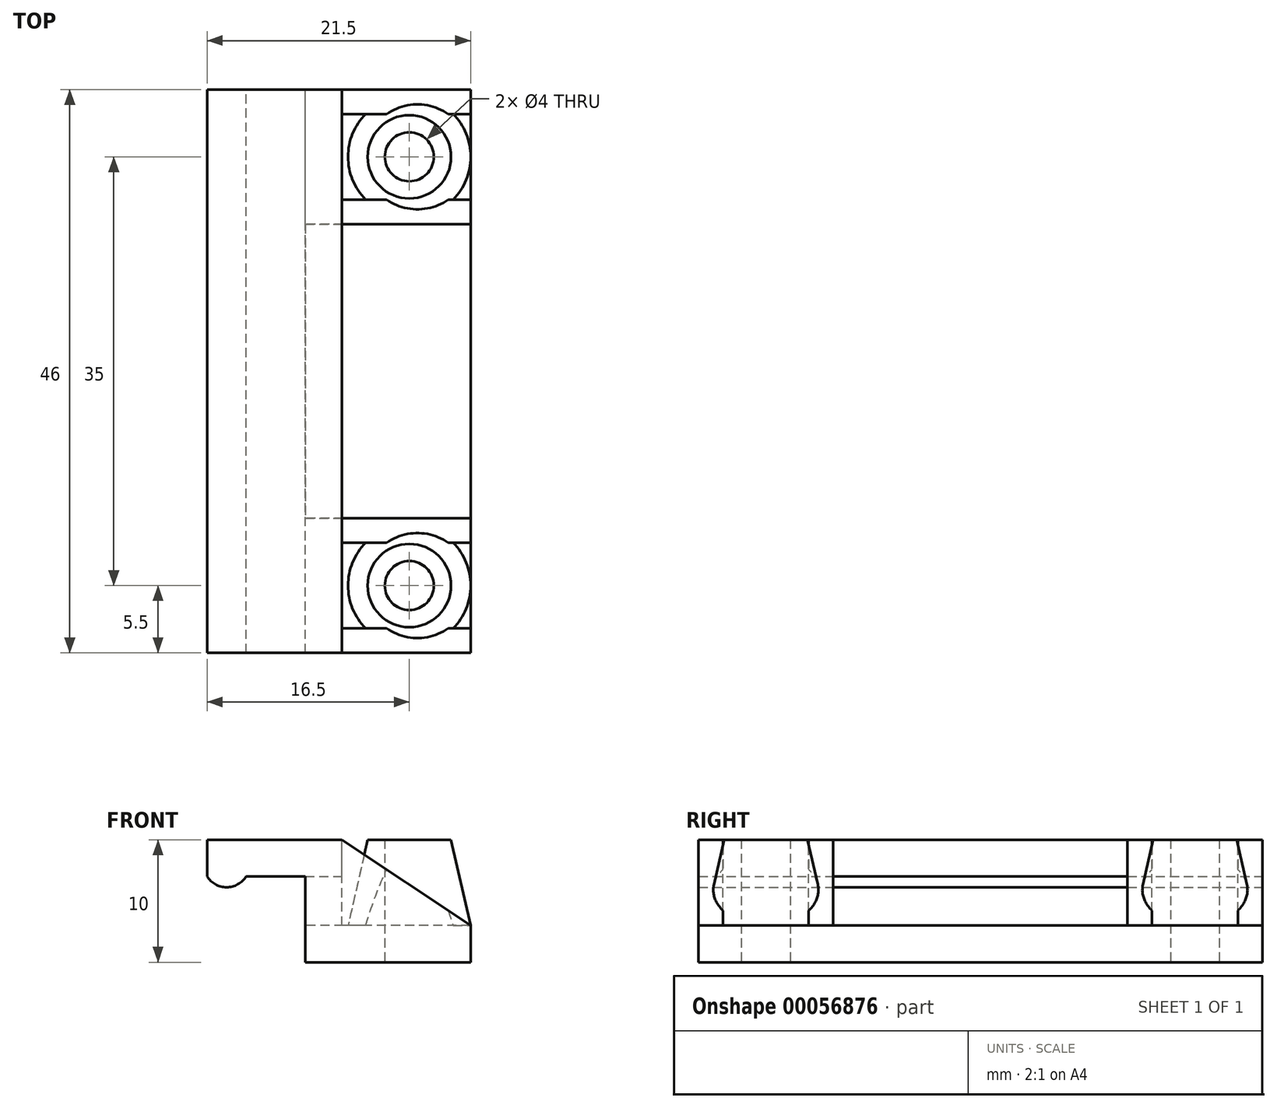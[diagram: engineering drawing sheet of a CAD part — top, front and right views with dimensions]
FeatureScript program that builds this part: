
annotation { "Feature Type Name" : "Feature", "Feature Type Description" : "" }
export const myFeature = defineFeature(function(context is Context, id is Id, definition is map)
    precondition{}
    {
        {
            var Q0;
            Q0=qCreatedBy(makeId("Front.planeOp"),FACE);
            var sketch = newSketch(context, id + "F0", { "sketchPlane" : qUnion([Q0])});
            skLineSegment(sketch, "E0", {"start": v(57.42, 0) * mm, "end": v(-61.71, 0) * mm, "construction": true});
            skLineSegment(sketch, "E1", {"start": v(0, 5) * mm, "end": v(0, -5) * mm, "construction": true});
            skLineSegment(sketch, "E2.0", {"start": v(12, 5) * mm, "end": v(-9.5, 5) * mm});
            skLineSegment(sketch, "E3.0", {"start": v(12, -5) * mm, "end": v(-9.5, -5) * mm});
            skPoint(sketch, "E4.orphan", {"position": v(0, 44.91) * mm});
            skLineSegment(sketch, "E5.0", {"start": v(-9.5, 5) * mm, "end": v(-9.5, -5) * mm, "construction": true});
            skLineSegment(sketch, "E6.0", {"start": v(12, 5) * mm, "end": v(12, -5) * mm, "construction": true});
            skLineSegment(sketch, "E7.0", {"start": v(1.5, 4) * mm, "end": v(1.5, -4) * mm, "construction": true});
            skLineSegment(sketch, "E8.0", {"start": v(-1.5, 4) * mm, "end": v(-1.5, -4) * mm, "construction": true});
            skLineSegment(sketch, "E9.0", {"start": v(57.42, 2) * mm, "end": v(-61.71, 2) * mm, "construction": true});
            skLineSegment(sketch, "E10.0", {"start": v(57.42, -2) * mm, "end": v(-61.71, -2) * mm, "construction": true});
            skLineSegment(sketch, "E11", {"start": v(12, -5) * mm, "end": v(12, -2) * mm});
            skLineSegment(sketch, "E12", {"start": v(12, -2) * mm, "end": v(1.5, -2) * mm});
            skLineSegment(sketch, "E13", {"start": v(1.5, -2) * mm, "end": v(1.5, 4) * mm});
            skLineSegment(sketch, "E14", {"start": v(-9.5, 5) * mm, "end": v(-9.5, 2) * mm});
            skLineSegment(sketch, "E15", {"start": v(-6.31, 2) * mm, "end": v(-1.5, 2) * mm});
            skLineSegment(sketch, "E16", {"start": v(-1.5, 2) * mm, "end": v(-1.5, -4) * mm});
            skLineSegment(sketch, "E17", {"start": v(-9.5, 2) * mm, "end": v(-9.5, 2) * mm});
            skLineSegment(sketch, "E18", {"start": v(1.5, 4) * mm, "end": v(1.5, 5) * mm});
            skLineSegment(sketch, "E19", {"start": v(1.5, 5) * mm, "end": v(1.5, -2) * mm});
            skLineSegment(sketch, "E20", {"start": v(-1.5, -4) * mm, "end": v(-1.5, -5) * mm});
            skLineSegment(sketch, "E21", {"start": v(1.5, 5) * mm, "end": v(12, -2) * mm});
            skArc(sketch, "E22", {"start": v(-9.5, 2) * mm, "mid": v(-7.9, 1.12) * mm, "end": v(-6.31, 2) * mm});
            skLineSegment(sketch, "E23", {"start": v(-1.5, 2) * mm, "end": v(1.5, 2) * mm});
            skLineSegment(sketch, "E24", {"start": v(1.5, -2) * mm, "end": v(-1.5, -2) * mm});
            skLineSegment(sketch, "E25.trimOffspring", {"start": v(1.5, -4) * mm, "end": v(1.5, -5) * mm});
            skSolve(sketch);
        }
        {
            var Q0;
            {var subQ0=sQuery(id+"F0.wireOp",EDGE,"E11");Q0=makeQuery(id+"F0.imprint","IMPRINT",FACE,{"disambiguationData":[TD([[makeQuery(id+"F0.imprint","IMPRINT",EDGE,{"derivedFrom":subQ0}),1.0]])]});}
            var Q1;
            {var subQ0=sQuery(id+"F0.wireOp",EDGE,"E14");Q1=makeQuery(id+"F0.imprint","IMPRINT",FACE,{"disambiguationData":[TD([[makeQuery(id+"F0.imprint","IMPRINT",EDGE,{"derivedFrom":subQ0}),1.0]])]});}
            var Q2;
            {var subQ0=sQuery(id+"F0.wireOp",EDGE,"E23");Q2=makeQuery(id+"F0.imprint","IMPRINT",FACE,{"disambiguationData":[TD([[makeQuery(id+"F0.imprint","IMPRINT",EDGE,{"derivedFrom":subQ0}),-1.0]])]});}
            extrude(context, id + "F1", {"entities" : qUnion([Q0, Q1, Q2]), "depth" : 11 * mm});
        }
        {
            var Q0;
            Q0=makeQuery(id+"F0.imprint","IMPRINT",FACE,{"disambiguationData":[TD([[makeQuery(id+"F0.imprint","IMPRINT",EDGE,{"derivedFrom":sQuery(id+"F0.wireOp",EDGE,"E12")}),-1.0]])]});
            extrude(context, id + "F2", {"entities" : qUnion([Q0]), "operationType" : NewBodyOperationType.ADD, "depth" : 2 * mm});
        }
        {
            var Q0;
            Q0=makeQuery(id+"F1.opExtrude","CAP_FACE",FACE,{"disambiguationData":[OSD([sQuery(id+"F0.wireOp",EDGE,"E2.0"),sQuery(id+"F0.wireOp",EDGE,"E3.0"),sQuery(id+"F0.wireOp",EDGE,"E11"),sQuery(id+"F0.wireOp",EDGE,"E12"),sQuery(id+"F0.wireOp",EDGE,"E14"),sQuery(id+"F0.wireOp",EDGE,"E15"),sQuery(id+"F0.wireOp",EDGE,"E16"),sQuery(id+"F0.wireOp",EDGE,"E19"),sQuery(id+"F0.wireOp",EDGE,"E20"),sQuery(id+"F0.wireOp",EDGE,"E22")])],"isStart":false});
            var sketch = newSketch(context, id + "F3", { "sketchPlane" : qUnion([Q0])});
            skLineSegment(sketch, "E26.0.0", {"start": v(-1.5, -5) * mm, "end": v(12, -5) * mm});
            skLineSegment(sketch, "E26.0.1", {"start": v(12, -5) * mm, "end": v(12, -2) * mm});
            skLineSegment(sketch, "E26.0.2", {"start": v(12, -2) * mm, "end": v(1.5, -2) * mm});
            skLineSegment(sketch, "E26.0.3", {"start": v(1.5, -2) * mm, "end": v(1.5, 5) * mm});
            skLineSegment(sketch, "E26.0.4", {"start": v(1.5, 5) * mm, "end": v(-9.5, 5) * mm});
            skLineSegment(sketch, "E26.0.5", {"start": v(-9.5, 5) * mm, "end": v(-9.5, 2) * mm});
            skArc(sketch, "E26.0.6", {"start": v(-9.5, 2) * mm, "mid": v(-7.9, 1.12) * mm, "end": v(-6.31, 2) * mm});
            skLineSegment(sketch, "E26.0.7", {"start": v(-6.31, 2) * mm, "end": v(-1.5, 2) * mm});
            skLineSegment(sketch, "E26.0.8", {"start": v(-1.5, 2) * mm, "end": v(-1.5, -5) * mm});
            skLineSegment(sketch, "E27", {"start": v(1.5, 5) * mm, "end": v(12, -2) * mm});
            skLineSegment(sketch, "E28", {"start": v(1.5, -2) * mm, "end": v(12, -2) * mm});
            skSolve(sketch);
        }
        {
            var Q0;
            Q0=makeQuery(id+"F3.imprint","IMPRINT",FACE,{"disambiguationData":[TD([[makeQuery(id+"F3.imprint","IMPRINT",EDGE,{"derivedFrom":sQuery(id+"F3.wireOp",EDGE,"E27")}),-1.0]])]});
            extrude(context, id + "F4", {"entities" : qUnion([Q0]), "operationType" : NewBodyOperationType.ADD, "oppositeDirection" : true, "depth" : 2 * mm});
        }
        {
            var Q0;
            Q0=makeQuery(id+"F1.opExtrude","SWEPT_FACE",FACE,{"disambiguationData":[OSD([sQuery(id+"F0.wireOp",EDGE,"E3.0")])]});
            var sketch = newSketch(context, id + "F5", { "sketchPlane" : qUnion([Q0])});
            skLineSegment(sketch, "E29.0.0", {"start": v(-1.5, 0) * mm, "end": v(12, 0) * mm});
            skLineSegment(sketch, "E29.0.1", {"start": v(12, 0) * mm, "end": v(12, 11) * mm});
            skLineSegment(sketch, "E29.0.2", {"start": v(12, 11) * mm, "end": v(-1.5, 11) * mm});
            skLineSegment(sketch, "E29.0.3", {"start": v(-1.5, 11) * mm, "end": v(-1.5, 0) * mm});
            skLineSegment(sketch, "E30", {"start": v(12, 5.5) * mm, "end": v(-1.5, 5.5) * mm, "construction": true});
            skLineSegment(sketch, "E31.0", {"start": v(7, 0) * mm, "end": v(7, 11) * mm, "construction": true});
            skCircle(sketch, "E32", {"center": v(7, 5.5) * mm, "radius": 2 * mm});
            skPoint(sketch, "E33.0", {"position": v(0, 0) * mm});
            skSolve(sketch);
        }
        {
            var Q0;
            Q0=makeQuery(id+"F5.imprint","IMPRINT",FACE,{"disambiguationData":[TD([[makeQuery(id+"F5.imprint","IMPRINT",EDGE,{"derivedFrom":sQuery(id+"F5.wireOp",EDGE,"E32")}),1.0]])]});
            extrude(context, id + "F6", {"entities" : qUnion([Q0]), "operationType" : NewBodyOperationType.REMOVE, "oppositeDirection" : true, "depth" : 25 * mm});
        }
        {
            var Q0;
            Q0=makeQuery(id+"F1.opExtrude","SWEPT_FACE",FACE,{"disambiguationData":[OSD([sQuery(id+"F0.wireOp",EDGE,"E12")])]});
            var sketch = newSketch(context, id + "F7", { "sketchPlane" : qUnion([Q0])});
            skCircle(sketch, "E34.0", {"center": v(7, -5.5) * mm, "radius": 2 * mm});
            skCircle(sketch, "E35", {"center": v(7, -5.5) * mm, "radius": 5 * mm});
            skCircle(sketch, "E36", {"center": v(7, -5.5) * mm, "radius": 3.4 * mm});
            skSolve(sketch);
        }
        {
            var Q0;
            Q0=makeQuery(id+"F7.imprint","IMPRINT",FACE,{"disambiguationData":[TD([[makeQuery(id+"F7.imprint","IMPRINT",EDGE,{"derivedFrom":sQuery(id+"F7.wireOp",EDGE,"E34.0")}),1.0]])]});
            extrude(context, id + "F8", {"entities" : qUnion([Q0]), "operationType" : NewBodyOperationType.ADD, "depth" : 7 * mm});
        }
        {
            var Q0;
            Q0=qCreatedBy(makeId("Right.planeOp"),FACE);
            cPlane(context, id + "F9", {"entities" : qUnion([Q0]), "cplaneType" : CPlaneType.OFFSET, "offset" : 7 * mm, "width" : 150 * mm, "height" : 150 * mm});
        }
        {
            var Q0;
            Q0=qCreatedBy(id+"F9.planeOp",FACE);
            var sketch = newSketch(context, id + "F10", { "sketchPlane" : qUnion([Q0])});
            skLineSegment(sketch, "E37.0", {"start": v(-3.5, -5) * mm, "end": v(-7.5, -5) * mm});
            skLineSegment(sketch, "E38.0", {"start": v(-8.9, -2) * mm, "end": v(-2.1, -2) * mm});
            skLineSegment(sketch, "E39.0", {"start": v(-9, -2) * mm, "end": v(-2, -2) * mm});
            skLineSegment(sketch, "E40.0", {"start": v(-10.5, -2) * mm, "end": v(-0.5, -2) * mm});
            skPoint(sketch, "E41.0", {"position": v(-5.5, -2) * mm});
            skLineSegment(sketch, "E42", {"start": v(-5.5, -2) * mm, "end": v(9, -2) * mm});
            skLineSegment(sketch, "E43.0.0", {"start": v(-8.9, 5) * mm, "end": v(-2.1, 5) * mm});
            skLineSegment(sketch, "E44", {"start": v(-2.1, 5) * mm, "end": v(-0.5, -2) * mm});
            skLineSegment(sketch, "E45", {"start": v(-2.1, -2) * mm, "end": v(-2.1, 5) * mm});
            skLineSegment(sketch, "E46", {"start": v(-2.1, -2) * mm, "end": v(-0.5, -2) * mm});
            skLineSegment(sketch, "E47", {"start": v(-5.5, -2) * mm, "end": v(-5.5, 5.43) * mm});
            skPoint(sketch, "E47.endSnap0", {"position": v(-5.5, 5) * mm});
            skSolve(sketch);
        }
        {
            var Q0;
            {var subQ0=sQuery(id+"F10.wireOp",EDGE,"E44");Q0=makeQuery(id+"F10.imprint","IMPRINT",FACE,{"disambiguationData":[TD([[makeQuery(id+"F10.imprint","IMPRINT",EDGE,{"derivedFrom":subQ0}),-1.0]])]});}
            var Q1;
            Q1=sQuery(id+"F10.wireOp",EDGE,"E47");
            revolve(context, id + "F11", {"operationType" : NewBodyOperationType.ADD, "entities" : qUnion([Q0]), "axis" : qUnion([Q1]), "revolveType" : RevolveType.FULL});
        }
        {
            var Q0;
            Q0=makeQuery(id+"F1.opExtrude","SWEPT_BODY",BODY,{"disambiguationData":[OSD([sQuery(id+"F0.wireOp",EDGE,"E2.0"),sQuery(id+"F0.wireOp",EDGE,"E3.0"),sQuery(id+"F0.wireOp",EDGE,"E11"),sQuery(id+"F0.wireOp",EDGE,"E12"),sQuery(id+"F0.wireOp",EDGE,"E14"),sQuery(id+"F0.wireOp",EDGE,"E15"),sQuery(id+"F0.wireOp",EDGE,"E16"),sQuery(id+"F0.wireOp",EDGE,"E19"),sQuery(id+"F0.wireOp",EDGE,"E20"),sQuery(id+"F0.wireOp",EDGE,"E22")])]});
            transform(context, id + "F12", {"entities" : qUnion([Q0]), "transformType" : TransformType.TRANSLATION_3D, "dx" : 0 * mm, "dy" : 35 * mm, "dz" : 0 * mm, "makeCopy" : true});
        }
        {
            var Q0;
            {var subQ0=sQuery(id+"F0.wireOp",EDGE,"E11");Q0=makeQuery(id+"F0.imprint","IMPRINT",FACE,{"disambiguationData":[TD([[makeQuery(id+"F0.imprint","IMPRINT",EDGE,{"derivedFrom":subQ0}),1.0]])]});}
            var Q1;
            {var subQ4=sQuery(id+"F0.wireOp",EDGE,"E14");Q1=makeQuery(id+"F0.imprint","IMPRINT",FACE,{"disambiguationData":[TD([[makeQuery(id+"F0.imprint","IMPRINT",EDGE,{"derivedFrom":subQ4}),1.0]])]});}
            extrude(context, id + "F13", {"entities" : qUnion([Q0, Q1]), "operationType" : NewBodyOperationType.ADD, "oppositeDirection" : true, "depth" : 24 * mm});
        }
    });
